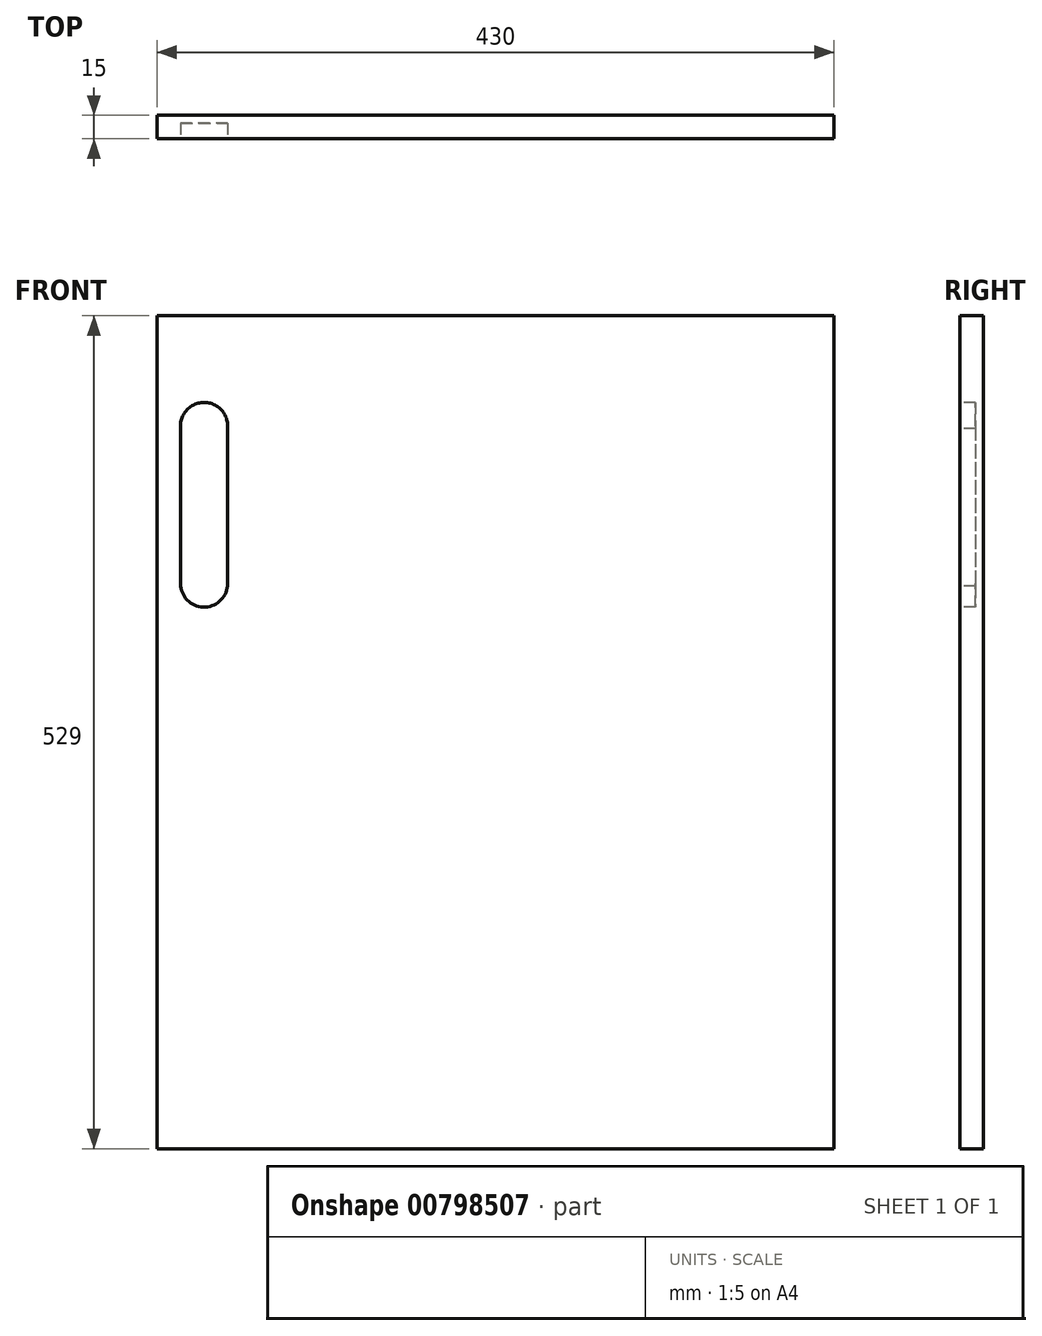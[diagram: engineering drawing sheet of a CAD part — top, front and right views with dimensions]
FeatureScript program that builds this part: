
annotation { "Feature Type Name" : "Feature", "Feature Type Description" : "" }
export const myFeature = defineFeature(function(context is Context, id is Id, definition is map)
    precondition{}
    {
        {
            var Q0;
            Q0=qCreatedBy(makeId("Front.planeOp"),FACE);
            var sketch = newSketch(context, id + "F0", { "sketchPlane" : qUnion([Q0])});
            skLineSegment(sketch, "E0.bottom", {"start": v(0, 0) * mm, "end": v(430, 0) * mm});
            skLineSegment(sketch, "E0.top", {"start": v(0, -529) * mm, "end": v(430, -529) * mm});
            skLineSegment(sketch, "E0.left", {"start": v(0, 0) * mm, "end": v(0, -529) * mm});
            skLineSegment(sketch, "E0.right", {"start": v(430, 0) * mm, "end": v(430, -529) * mm});
            skLineSegment(sketch, "E1", {"start": v(0, -90) * mm, "end": v(325.17, -90) * mm, "construction": true});
            skSolve(sketch);
        }
        {
            var Q0;
            Q0=makeQuery(id+"F0.imprint","IMPRINT",FACE,{"disambiguationData":[TD([[makeQuery(id+"F0.imprint","IMPRINT",EDGE,{"derivedFrom":sQuery(id+"F0.wireOp",EDGE,"E0.bottom")}),-1.0]])]});
            extrude(context, id + "F1", {"entities" : qUnion([Q0]), "depth" : 15 * mm, "offsetDistance" : 25 * mm});
        }
        {
            var Q0;
            Q0=makeQuery(id+"F1.opExtrude","CAP_FACE",FACE,{"disambiguationData":[OSD([sQuery(id+"F0.wireOp",EDGE,"E0.bottom"),sQuery(id+"F0.wireOp",EDGE,"E0.top"),sQuery(id+"F0.wireOp",EDGE,"E0.left"),sQuery(id+"F0.wireOp",EDGE,"E0.right")])],"isStart":false});
            var sketch = newSketch(context, id + "F2", { "sketchPlane" : qUnion([Q0])});
            skCircle(sketch, "E2", {"center": v(30, -70) * mm, "radius": 15 * mm});
            skCircle(sketch, "E3", {"center": v(30, -170) * mm, "radius": 15 * mm});
            skLineSegment(sketch, "E4", {"start": v(15.1, -71.66) * mm, "end": v(15.1, -171.66) * mm});
            skLineSegment(sketch, "E5", {"start": v(45, -69.88) * mm, "end": v(45, -171.66) * mm});
            skSolve(sketch);
        }
        {
            var Q0;
            {var subQ0=sQuery(id+"F2.wireOp",EDGE,"E2");var subQ1=makeQuery(id+"F2.imprint","INTERSECT",VERTEX,{"derivedFrom":[subQ0,sQuery(id+"F2.wireOp",EDGE,"E4")]});Q0=makeQuery(id+"F2.imprint","IMPRINT",FACE,{"disambiguationData":[TD([[makeQuery(id+"F2.imprint","IMPRINT",EDGE,{"disambiguationData":[TD([[subQ1,1.0]])],"derivedFrom":subQ0}),1.0]])]});}
            var Q1;
            {var subQ0=sQuery(id+"F2.wireOp",EDGE,"E4");var subQ1=sQuery(id+"F2.wireOp",EDGE,"E2");var subQ2=makeQuery(id+"F2.imprint","INTERSECT",VERTEX,{"derivedFrom":[subQ1,subQ0]});Q1=makeQuery(id+"F2.imprint","IMPRINT",FACE,{"disambiguationData":[TD([[makeQuery(id+"F2.imprint","IMPRINT",EDGE,{"disambiguationData":[TD([[subQ2,-1.0]])],"derivedFrom":subQ1}),-1.0]])]});}
            var Q2;
            {var subQ0=sQuery(id+"F2.wireOp",EDGE,"E3");var subQ1=makeQuery(id+"F2.imprint","INTERSECT",VERTEX,{"derivedFrom":[subQ0,sQuery(id+"F2.wireOp",EDGE,"E5")]});Q2=makeQuery(id+"F2.imprint","IMPRINT",FACE,{"disambiguationData":[TD([[makeQuery(id+"F2.imprint","IMPRINT",EDGE,{"disambiguationData":[TD([[subQ1,-1.0]])],"derivedFrom":subQ0}),1.0]])]});}
            extrude(context, id + "F3", {"entities" : qUnion([Q0, Q1, Q2]), "operationType" : NewBodyOperationType.REMOVE, "oppositeDirection" : true, "depth" : 10 * mm, "offsetDistance" : 25 * mm});
        }
    });
